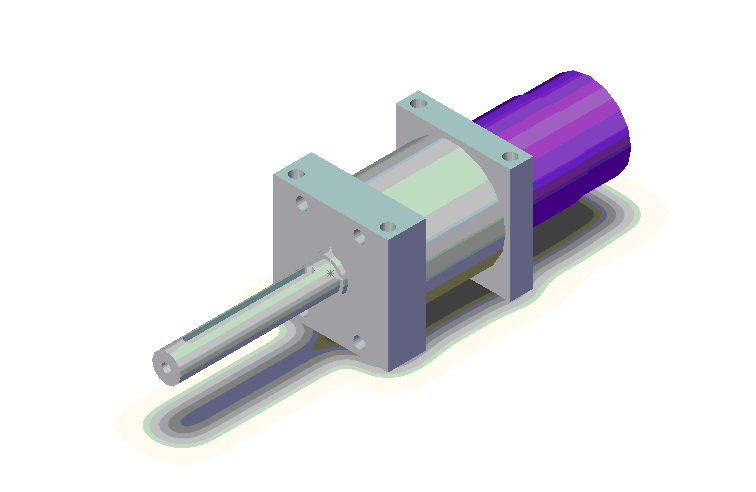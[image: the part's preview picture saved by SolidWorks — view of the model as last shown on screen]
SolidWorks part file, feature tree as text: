
SOLIDWORKS PART (.sldprt)
format: sldprt  version: not decoded by parser v0  size: 541,184 bytes
history: native  units: mm
features: sketch x14, extrude x7, cut_extrude x7, plane x2 (+8 scaffold rows collapsed)
feature tree (38):
  scaffold x8  (default folders/planes/origin — collapsed)
  sketch  "Sketch1"  dims[D13=4.0mm D14=4.0mm D15=4.0mm D16=4.0mm D1=19.05mm D2=38.1mm D3=19.05mm D4=38.1mm D5=9.525mm D6=9.53mm D7=9.53mm D8=9.53mm D9=3.81mm D10=3.81mm D11=34.29mm D12=34.29mm]
  extrude  "Base-Extrude"  Depth=12.7mm
  sketch  "Sketch2"  dims[D1=9.525mm]
  extrude  "Boss-Extrude1"  Depth=54.61mm
  plane  "Plane1"
  sketch  "Sketch3"  dims[D1=3.175mm D2=3.175mm D3=7.62mm D4=39.37mm]
  plane  "Plane2"  Offset=2.7625mm
  cut_extrude  "Cut-Extrude3"  [1 undecoded]
  sketch  "Sketch4"  dims[D1=3.0mm]
  cut_extrude  "Cut-Extrude4"  Depth=9.525mm
  sketch  "Sketch5"
  extrude  "Boss-Extrude2"  Depth=1.5mm
  sketch  "Sketch6"  dims[D1=4.0mm D2=4.0mm D3=3.81mm D4=34.29mm D5=3.81mm D6=3.81mm]
  cut_extrude  "Cut-Extrude5"  Depth=9.5mm
  sketch  "Sketch7"  dims[D1=15.24mm]
  cut_extrude  "Cut-Extrude6"  Depth=9.5mm
  sketch  "Sketch8"  dims[D1=35.0mm]
  extrude  "Boss-Extrude3"  Depth=27.94mm
  sketch  "Sketch9"
  extrude  "Boss-Extrude4"  Depth=7.62mm
  sketch  "Sketch11"  dims[D7=4.0mm D8=4.0mm D9=4.0mm D10=4.0mm D11=4.0mm D12=4.0mm D13=4.0mm D14=4.0mm D1=9.525mm D2=9.525mm D3=28.575mm D4=28.575mm D5=3.81mm D6=34.29mm D15=3.81mm D16=34.29mm D17=9.53mm D18=28.58mm]
  cut_extrude  "Cut-Extrude7"  Depth=9.525mm
  sketch  "Sketch12"  dims[c1.D3=4.0mm c1.D4=4.0mm c1.D1=3.81mm c1.D2=3.81mm c2.D3=3.81mm c2.D5=3.81mm]
  cut_extrude  "Cut-Extrude8"  Depth=9.525mm
  sketch  "Sketch13"
  cut_extrude  "Cut-Extrude9"  Depth=9.525mm
  sketch  "Sketch14"  dims[D1=27.7mm]
  extrude  "Boss-Extrude5"  Depth=37.8mm
  sketch  "Sketch15"  dims[D1=28.956mm]
  extrude  "Boss-Extrude6"  Depth=23mm
decode coverage: 24 of 28 modeling features carry decoded parameters
note: 1 parameter value undecoded
note: suppression state not decoded; provenance and decode notes live in map.json
